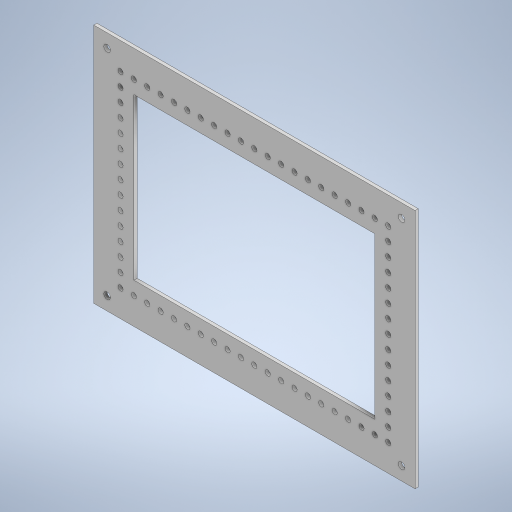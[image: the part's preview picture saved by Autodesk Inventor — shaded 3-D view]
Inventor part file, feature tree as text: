
AUTODESK INVENTOR PART (.ipt)
format: ipt  version: 2023.4 (Build 274418000, 418)  size: 387,072 bytes
history: native  units: in
note: dims shown in document units (in); Inventor stores cm internally (conversion verified against a paired STEP export)
features: sketch x3, extrude x2, sheet_metal_op x1, other x1
ambient origin geometry x8: Origin, YZ Plane, XZ Plane, XY Plane, X Axis, Y Axis, Z Axis, Center Point
bodies: Solid1 (feature_tree)
feature tree (7):
  sheet_metal_op  "Face1"
  extrude  "Extrusion1"  Depth=6.0in
  extrude  "Extrusion2"  Depth=0.12in
  sketch  "Sketch1"  dims[d0=9.0in d1=6.0in]
  other  "Plate1"
  sketch  "Sketch2"  dims[d2=1.5in d3=0.12in]
  sketch  "Sketch3"  dims[d4=0.197in d6=0.5in d7=0.5in d8=7.874in d10=0.5in d11=0.3937in d13=1.0in d15=1.0in d16=0.0in d17=0.197in d18=1.0in d19=0.5in d20=5.5118in d22=0.5in d23=0.3937in d25=1.0in d27=0.197in d30=1.0in d31=0.5in d32=7.874in d34=0.5in d35=0.3937in d37=1.0in d39=0.197in d40=1.0in d41=0.5in d42=5.5118in d44=0.5in d45=0.3937in d47=1.0in d49=0.25in d50=0.5in d51=0.5in d52=0.25in d53=0.5in d54=0.5in d55=0.25in d56=0.5in d57=0.5in d58=0.25in d59=0.5in d60=0.5in d61=1.0in d62=0.0in]
